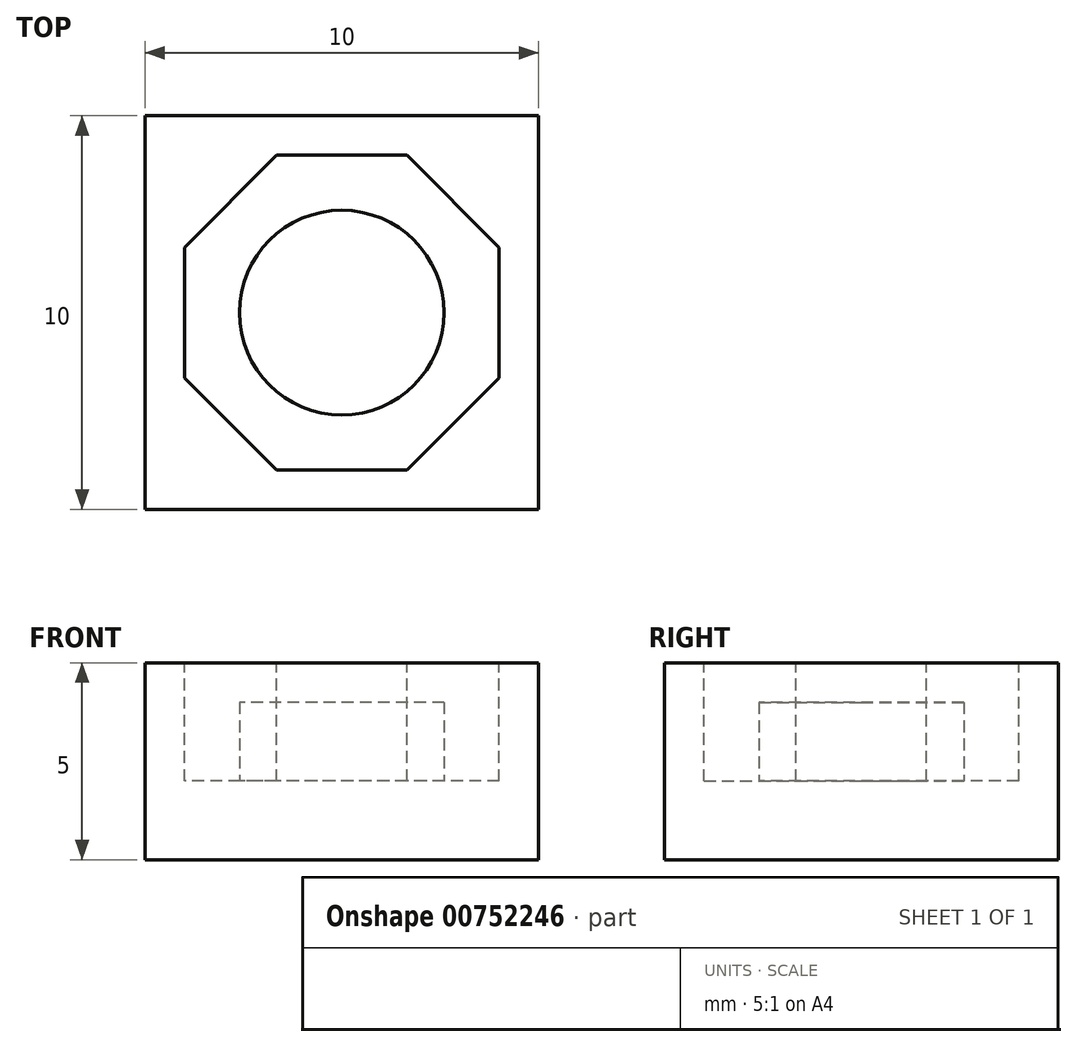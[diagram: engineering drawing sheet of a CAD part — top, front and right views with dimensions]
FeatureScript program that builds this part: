
annotation { "Feature Type Name" : "Feature", "Feature Type Description" : "" }
export const myFeature = defineFeature(function(context is Context, id is Id, definition is map)
    precondition{}
    {
        {
            var Q0;
            Q0=qCreatedBy(makeId("Top.planeOp"),FACE);
            var sketch = newSketch(context, id + "F0", { "sketchPlane" : qUnion([Q0])});
            skLineSegment(sketch, "E0.bottom", {"start": v(5, -5) * mm, "end": v(-5, -5) * mm});
            skLineSegment(sketch, "E0.top", {"start": v(5, 5) * mm, "end": v(-5, 5) * mm});
            skLineSegment(sketch, "E0.left", {"start": v(5, -5) * mm, "end": v(5, 5) * mm});
            skLineSegment(sketch, "E0.right", {"start": v(-5, -5) * mm, "end": v(-5, 5) * mm});
            skPoint(sketch, "E0.middle", {"position": v(0, 0) * mm});
            skSolve(sketch);
        }
        {
            var Q0;
            Q0=makeQuery(id+"F0.imprint","IMPRINT",FACE,{"disambiguationData":[TD([[makeQuery(id+"F0.imprint","IMPRINT",EDGE,{"derivedFrom":sQuery(id+"F0.wireOp",EDGE,"E0.bottom")}),-1.0]])]});
            extrude(context, id + "F1", {"entities" : qUnion([Q0]), "depth" : 5 * mm, "offsetDistance" : 25 * mm});
        }
        {
            var Q0;
            Q0=makeQuery(id+"F1.opExtrude","CAP_FACE",FACE,{"disambiguationData":[OSD([sQuery(id+"F0.wireOp",EDGE,"E0.bottom"),sQuery(id+"F0.wireOp",EDGE,"E0.top"),sQuery(id+"F0.wireOp",EDGE,"E0.left"),sQuery(id+"F0.wireOp",EDGE,"E0.right")])],"isStart":false});
            var sketch = newSketch(context, id + "F2", { "sketchPlane" : qUnion([Q0])});
            skCircle(sketch, "E1.cCircle", {"center": v(0, 0) * mm, "radius": 4 * mm, "construction": true});
            skLineSegment(sketch, "E1.0", {"start": v(-4, -1.66) * mm, "end": v(-4, 1.66) * mm});
            skLineSegment(sketch, "E1.1", {"start": v(-4, 1.66) * mm, "end": v(-1.66, 4) * mm});
            skLineSegment(sketch, "E1.2", {"start": v(-1.66, 4) * mm, "end": v(1.66, 4) * mm});
            skLineSegment(sketch, "E1.3", {"start": v(1.66, 4) * mm, "end": v(4, 1.66) * mm});
            skLineSegment(sketch, "E1.4", {"start": v(4, 1.66) * mm, "end": v(4, -1.66) * mm});
            skLineSegment(sketch, "E1.5", {"start": v(4, -1.66) * mm, "end": v(1.66, -4) * mm});
            skLineSegment(sketch, "E1.6", {"start": v(1.66, -4) * mm, "end": v(-1.66, -4) * mm});
            skLineSegment(sketch, "E1.7", {"start": v(-1.66, -4) * mm, "end": v(-4, -1.66) * mm});
            skPoint(sketch, "E1.0.midPoint", {"position": v(-4, 0) * mm});
            skSolve(sketch);
        }
        {
            var Q0;
            Q0 = qSketchRegion(id + "F2", true);
            extrude(context, id + "F3", {"entities" : qUnion([Q0]), "operationType" : NewBodyOperationType.REMOVE, "oppositeDirection" : true, "depth" : 3 * mm, "offsetDistance" : 25 * mm});
        }
        {
            var Q0;
            Q0=makeQuery(id+"F3.boolean.opBoolean","COPY",FACE,{"derivedFrom":makeQuery(id+"F3.opExtrude","CAP_FACE",FACE,{"disambiguationData":[OSD([sQuery(id+"F2.wireOp",EDGE,"E1.0"),sQuery(id+"F2.wireOp",EDGE,"E1.1"),sQuery(id+"F2.wireOp",EDGE,"E1.2"),sQuery(id+"F2.wireOp",EDGE,"E1.3"),sQuery(id+"F2.wireOp",EDGE,"E1.4"),sQuery(id+"F2.wireOp",EDGE,"E1.5"),sQuery(id+"F2.wireOp",EDGE,"E1.6"),sQuery(id+"F2.wireOp",EDGE,"E1.7")])],"isStart":false})});
            var sketch = newSketch(context, id + "F4", { "sketchPlane" : qUnion([Q0])});
            skCircle(sketch, "E2", {"center": v(0, 0) * mm, "radius": 2.6 * mm});
            skSolve(sketch);
        }
        {
            var Q0;
            Q0=makeQuery(id+"F4.imprint","IMPRINT",FACE,{"disambiguationData":[TD([[makeQuery(id+"F4.imprint","IMPRINT",EDGE,{"derivedFrom":sQuery(id+"F4.wireOp",EDGE,"E2")}),1.0]])]});
            extrude(context, id + "F5", {"entities" : qUnion([Q0]), "operationType" : NewBodyOperationType.ADD, "depth" : 2 * mm, "offsetDistance" : 25 * mm});
        }
    });
